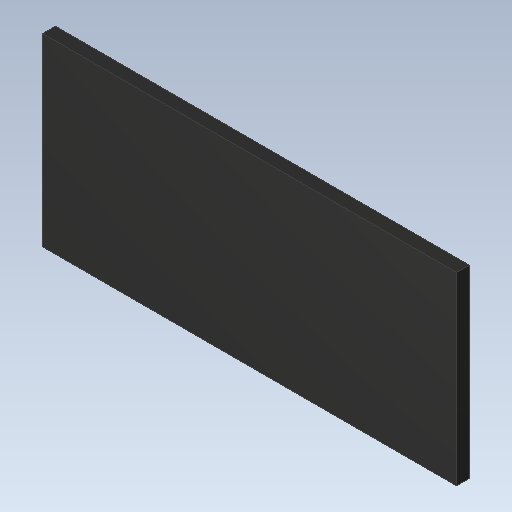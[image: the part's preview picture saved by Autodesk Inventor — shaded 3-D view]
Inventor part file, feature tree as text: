
AUTODESK INVENTOR PART (.ipt)
format: ipt  version: 2020 (Build 240168000, 168)  size: 86,528 bytes
history: imported  units: in
note: dims shown in document units (in); Inventor stores cm internally (conversion verified against a paired STEP export)
features: imported_body x1
ambient origin geometry x8: Origin, YZ Plane, XZ Plane, XY Plane, X Axis, Y Axis, Z Axis, Center Point
bodies: Solid1 (imported_parasolid), Body1 (imported_parasolid)
feature tree (1):
  imported_body  NMx_Import_Brep_tag  [imported B-rep: ~6 faces, bbox_mm=[3.2508, 1.4508, 0.1]]
